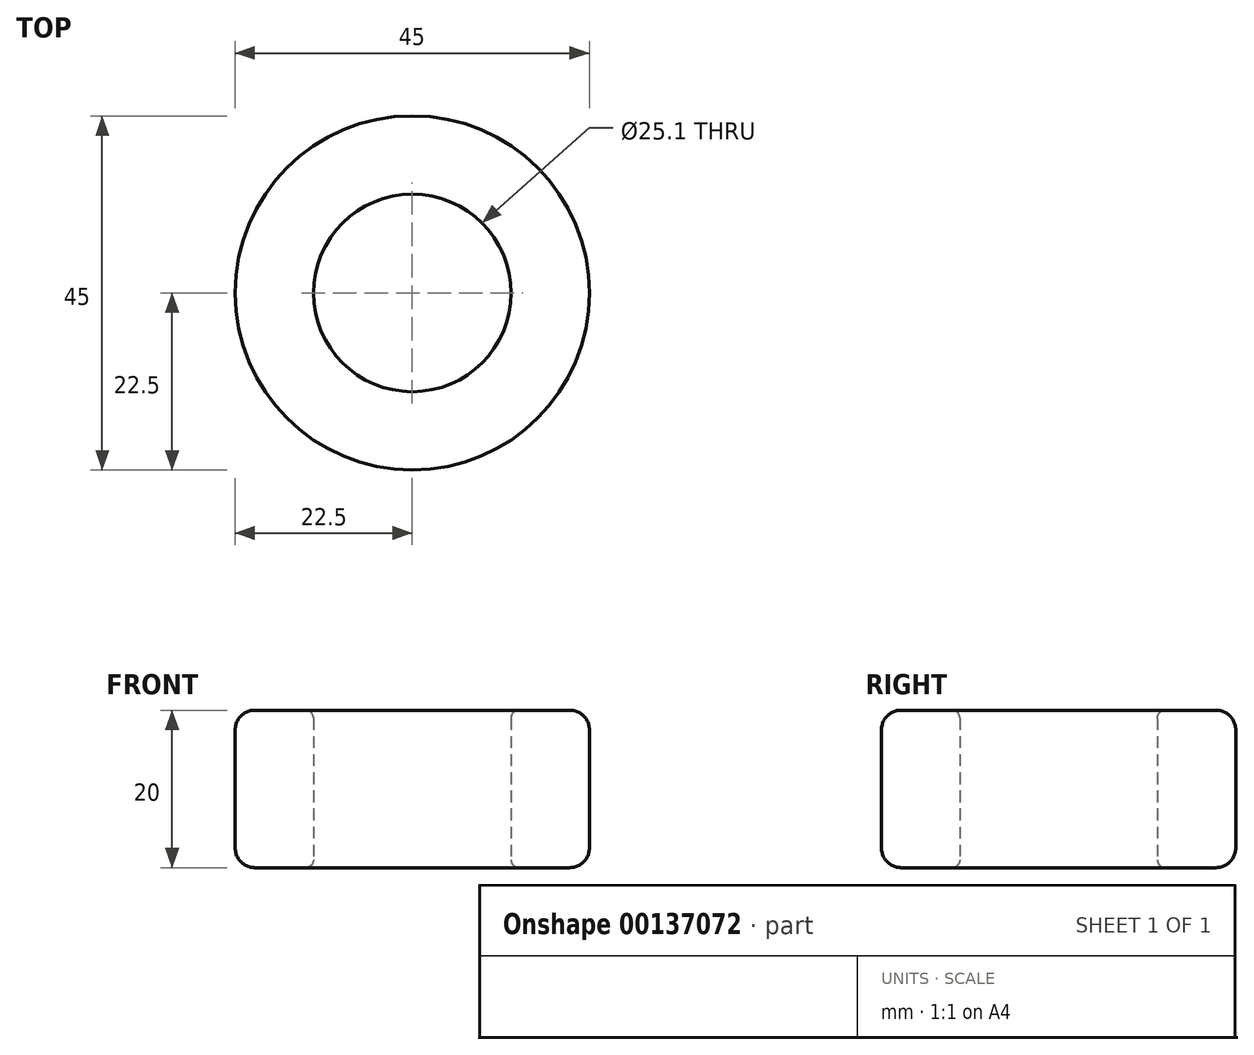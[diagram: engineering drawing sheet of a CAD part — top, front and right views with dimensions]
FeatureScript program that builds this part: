
annotation { "Feature Type Name" : "Feature", "Feature Type Description" : "" }
export const myFeature = defineFeature(function(context is Context, id is Id, definition is map)
    precondition{}
    {
        {
            var Q0;
            Q0=qCreatedBy(makeId("Top.planeOp"),FACE);
            var sketch = newSketch(context, id + "F0", { "sketchPlane" : qUnion([Q0])});
            skCircle(sketch, "E0", {"center": v(0, 0) * mm, "radius": 22.5 * mm});
            skCircle(sketch, "E1", {"center": v(0, 0) * mm, "radius": 12.55 * mm});
            skSolve(sketch);
        }
        {
            var Q0;
            Q0=makeQuery(id+"F0.imprint","IMPRINT",FACE,{"disambiguationData":[TD([[makeQuery(id+"F0.imprint","IMPRINT",EDGE,{"derivedFrom":sQuery(id+"F0.wireOp",EDGE,"E0")}),1.0]])]});
            extrude(context, id + "F1", {"entities" : qUnion([Q0]), "depth" : 20 * mm});
        }
        {
            var Q0;
            Q0=makeQuery(id+"F1.opExtrude","CAP_EDGE",EDGE,{"disambiguationData":[OSD([sQuery(id+"F0.wireOp",EDGE,"E0")])],"isStart":false});
            fillet(context, id + "F2", {"entities" : qUnion([Q0]), "radius" : 2.5 * mm, "tangentPropagation" : true, "allowEdgeOverflow" : false});
        }
        {
            var Q0;
            Q0=makeQuery(id+"F1.opExtrude","CAP_EDGE",EDGE,{"disambiguationData":[OSD([sQuery(id+"F0.wireOp",EDGE,"E1")])],"isStart":false});
            fillet(context, id + "F3", {"entities" : qUnion([Q0]), "radius" : 1 * mm, "tangentPropagation" : true, "allowEdgeOverflow" : false});
        }
        {
            var Q0;
            Q0=makeQuery(id+"F1.opExtrude","CAP_EDGE",EDGE,{"disambiguationData":[OSD([sQuery(id+"F0.wireOp",EDGE,"E1")])],"isStart":true});
            fillet(context, id + "F4", {"entities" : qUnion([Q0]), "radius" : 1 * mm, "tangentPropagation" : true, "allowEdgeOverflow" : false});
        }
        {
            var Q0;
            Q0=makeQuery(id+"F1.opExtrude","CAP_EDGE",EDGE,{"disambiguationData":[OSD([sQuery(id+"F0.wireOp",EDGE,"E0")])],"isStart":true});
            fillet(context, id + "F5", {"entities" : qUnion([Q0]), "radius" : 2.5 * mm, "tangentPropagation" : true, "allowEdgeOverflow" : false});
        }
    });
